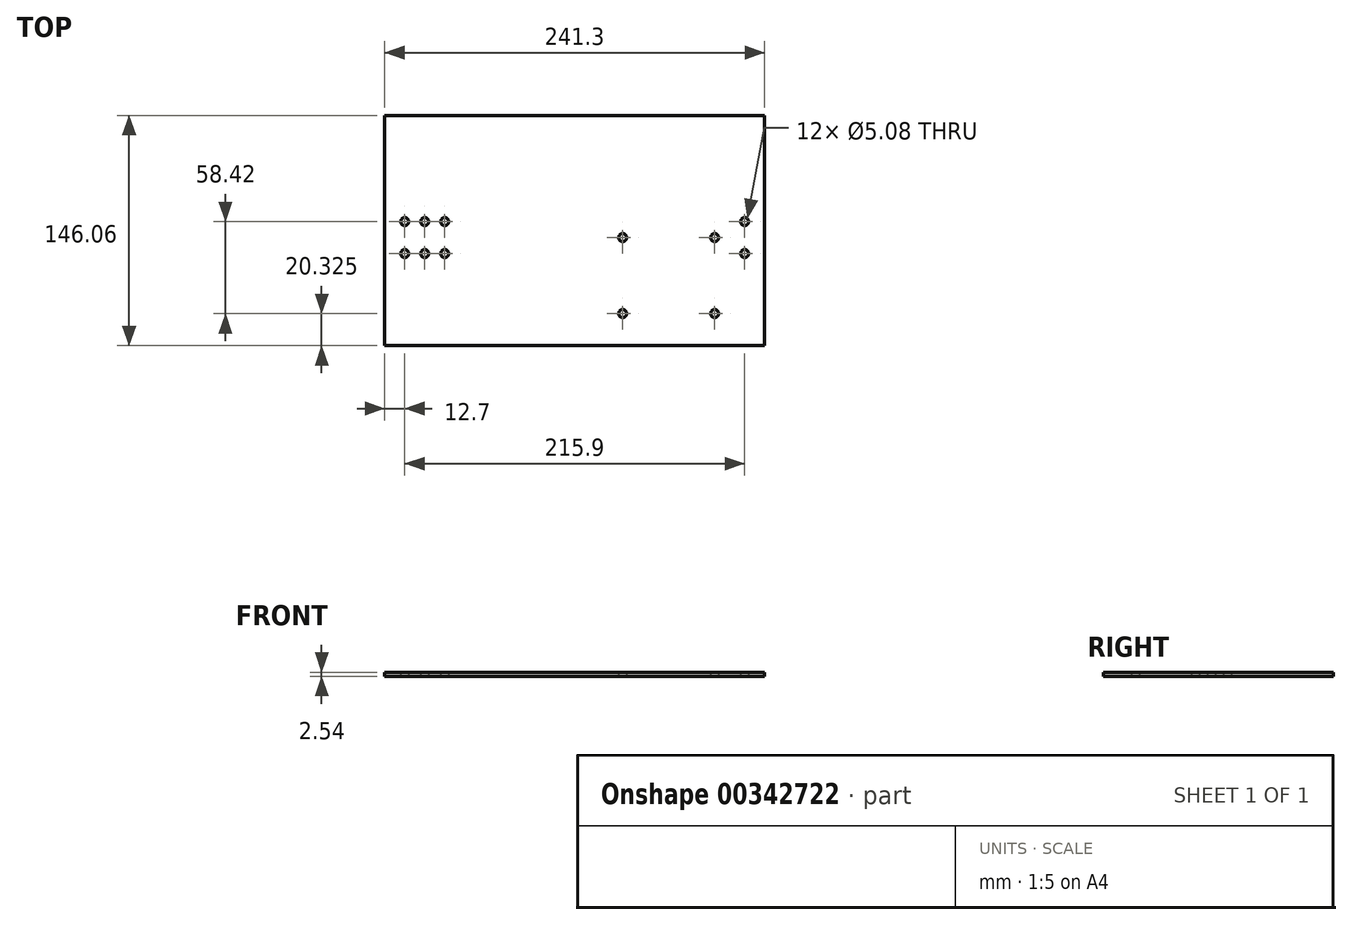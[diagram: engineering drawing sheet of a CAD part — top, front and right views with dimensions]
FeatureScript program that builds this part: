
annotation { "Feature Type Name" : "Feature", "Feature Type Description" : "" }
export const myFeature = defineFeature(function(context is Context, id is Id, definition is map)
    precondition{}
    {
        {
            var Q0;
            Q0=qCreatedBy(makeId("Top.planeOp"),FACE);
            var sketch = newSketch(context, id + "F0", { "sketchPlane" : qUnion([Q0])});
            skLineSegment(sketch, "E0.bottom", {"start": v(120.65, 73.03) * mm, "end": v(-120.65, 73.03) * mm});
            skLineSegment(sketch, "E0.top", {"start": v(120.65, -73.03) * mm, "end": v(-120.65, -73.03) * mm});
            skLineSegment(sketch, "E0.left", {"start": v(120.65, 73.02) * mm, "end": v(120.65, -73.03) * mm});
            skLineSegment(sketch, "E0.right", {"start": v(-120.65, 73.03) * mm, "end": v(-120.65, -73.03) * mm});
            skPoint(sketch, "E0.middle", {"position": v(0, 0) * mm});
            skCircle(sketch, "E1", {"center": v(107.95, 5.72) * mm, "radius": 2.54 * mm});
            skCircle(sketch, "E2", {"center": v(107.95, -14.6) * mm, "radius": 2.54 * mm});
            skCircle(sketch, "E3", {"center": v(88.9, -4.45) * mm, "radius": 2.54 * mm});
            skCircle(sketch, "E4", {"center": v(30.48, -4.45) * mm, "radius": 2.54 * mm});
            skCircle(sketch, "E5", {"center": v(30.48, -52.7) * mm, "radius": 2.54 * mm});
            skCircle(sketch, "E6", {"center": v(88.9, -52.7) * mm, "radius": 2.54 * mm});
            skCircle(sketch, "E7", {"center": v(-107.95, 5.71) * mm, "radius": 2.54 * mm});
            skCircle(sketch, "E8", {"center": v(-95.25, 5.71) * mm, "radius": 2.54 * mm});
            skCircle(sketch, "E9", {"center": v(-82.55, 5.71) * mm, "radius": 2.54 * mm});
            skCircle(sketch, "E10", {"center": v(-107.95, -14.6) * mm, "radius": 2.54 * mm});
            skCircle(sketch, "E11", {"center": v(-95.25, -14.6) * mm, "radius": 2.54 * mm});
            skCircle(sketch, "E12", {"center": v(-82.55, -14.6) * mm, "radius": 2.54 * mm});
            skLineSegment(sketch, "E13", {"start": v(-107.95, -14.6) * mm, "end": v(-95.25, -14.6) * mm, "construction": true});
            skLineSegment(sketch, "E14", {"start": v(-95.25, -14.6) * mm, "end": v(-82.55, -14.6) * mm, "construction": true});
            skLineSegment(sketch, "E15", {"start": v(107.95, 5.72) * mm, "end": v(107.95, -14.6) * mm, "construction": true});
            skLineSegment(sketch, "E16", {"start": v(88.9, -4.44) * mm, "end": v(107.95, -4.44) * mm, "construction": true});
            skSolve(sketch);
        }
        {
            var Q0;
            Q0 = qSketchRegion(id + "F0", true);
            extrude(context, id + "F1", {"entities" : qUnion([Q0]), "depth" : 2.54 * mm});
        }
    });
